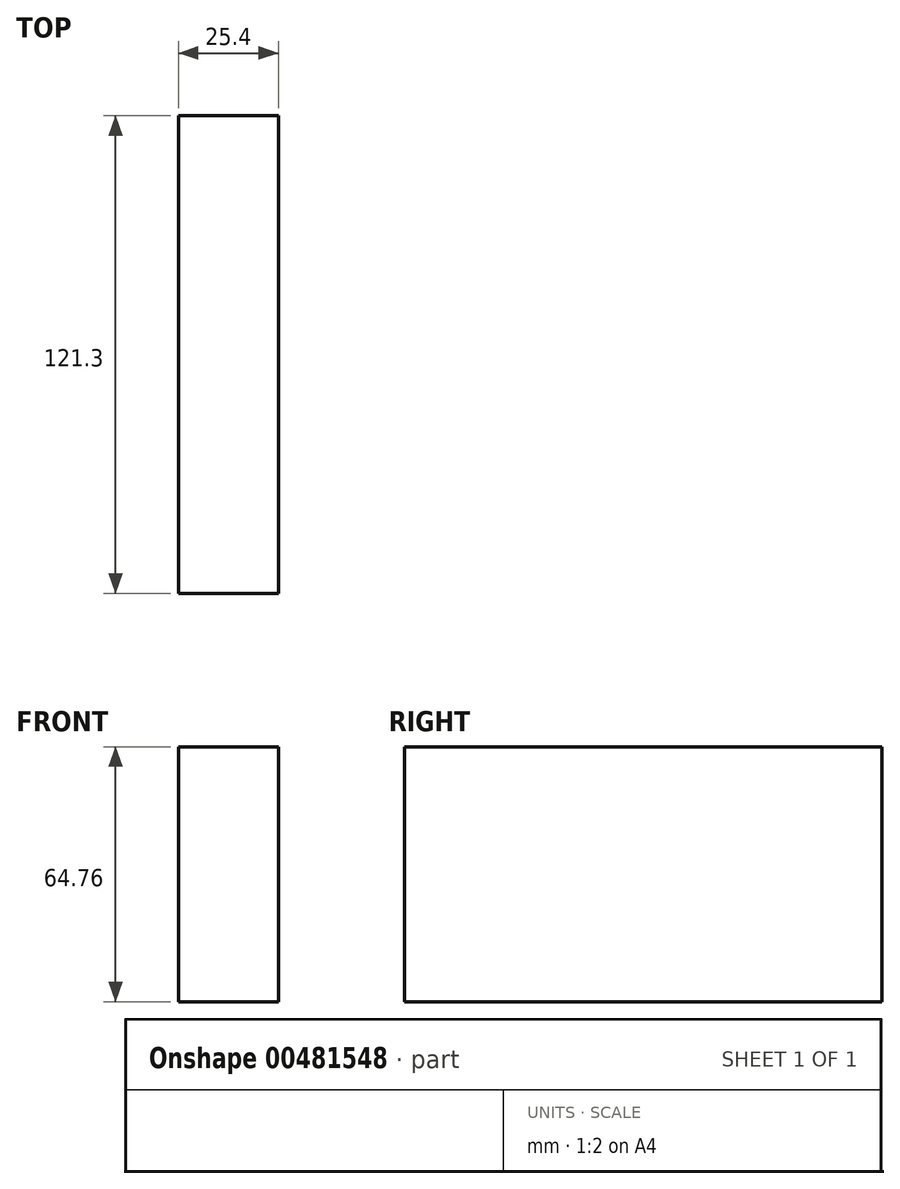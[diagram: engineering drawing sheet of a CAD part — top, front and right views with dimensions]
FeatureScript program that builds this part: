
annotation { "Feature Type Name" : "Feature", "Feature Type Description" : "" }
export const myFeature = defineFeature(function(context is Context, id is Id, definition is map)
    precondition{}
    {
        {
            var Q0;
            Q0=qCreatedBy(makeId("Right.planeOp"),FACE);
            var sketch = newSketch(context, id + "F0", { "sketchPlane" : qUnion([Q0])});
            skLineSegment(sketch, "E0.bottom", {"start": v(60.65, 32.38) * mm, "end": v(-60.65, 32.38) * mm});
            skLineSegment(sketch, "E0.top", {"start": v(60.65, -32.38) * mm, "end": v(-60.65, -32.38) * mm});
            skLineSegment(sketch, "E0.left", {"start": v(60.65, 32.38) * mm, "end": v(60.65, -32.38) * mm});
            skLineSegment(sketch, "E0.right", {"start": v(-60.65, 32.38) * mm, "end": v(-60.65, -32.38) * mm});
            skPoint(sketch, "E0.middle", {"position": v(0, 0) * mm});
            skSolve(sketch);
        }
        {
            var Q0;
            Q0 = qSketchRegion(id + "F0", true);
            extrude(context, id + "F1", {"entities" : qUnion([Q0]), "depth" : 25.4 * mm});
        }
    });
